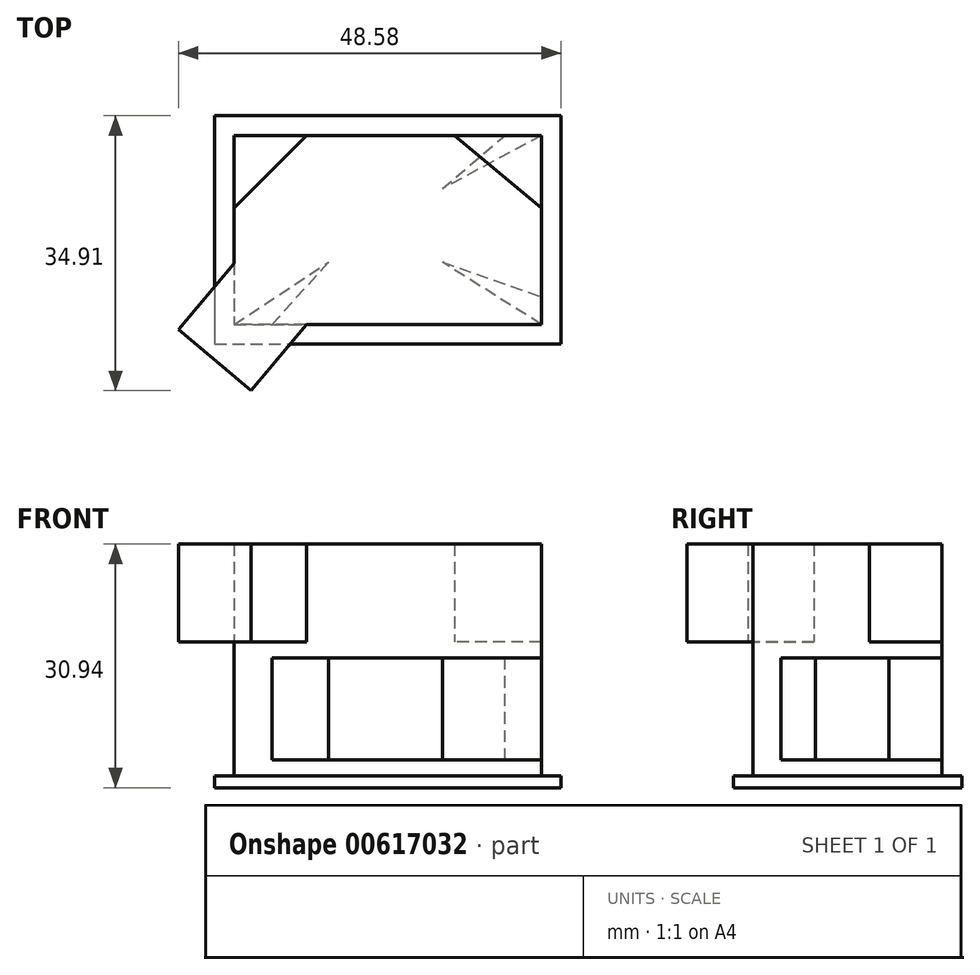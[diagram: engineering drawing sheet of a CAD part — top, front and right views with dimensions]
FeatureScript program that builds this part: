
annotation { "Feature Type Name" : "Feature", "Feature Type Description" : "" }
export const myFeature = defineFeature(function(context is Context, id is Id, definition is map)
    precondition{}
    {
        {
            var Q0;
            Q0=qCreatedBy(makeId("Top.planeOp"),FACE);
            var sketch = newSketch(context, id + "F0", { "sketchPlane" : qUnion([Q0])});
            skLineSegment(sketch, "E0.bottom", {"start": v(-14.47, 23) * mm, "end": v(29.53, 23) * mm});
            skLineSegment(sketch, "E0.top", {"start": v(-14.47, -6) * mm, "end": v(29.53, -6) * mm});
            skLineSegment(sketch, "E0.left", {"start": v(-14.47, 23) * mm, "end": v(-14.47, -6) * mm});
            skLineSegment(sketch, "E0.right", {"start": v(29.53, 23) * mm, "end": v(29.53, -6) * mm});
            skSolve(sketch);
        }
        {
            var Q0;
            Q0 = qSketchRegion(id + "F0", true);
            extrude(context, id + "F1", {"entities" : qUnion([Q0]), "depth" : 1.5 * mm, "offsetDistance" : 25 * mm});
        }
        {
            var Q0;
            Q0=makeQuery(id+"F1.opExtrude","CAP_FACE",FACE,{"disambiguationData":[OSD([sQuery(id+"F0.wireOp",EDGE,"E0.bottom"),sQuery(id+"F0.wireOp",EDGE,"E0.top"),sQuery(id+"F0.wireOp",EDGE,"E0.left"),sQuery(id+"F0.wireOp",EDGE,"E0.right")])],"isStart":false});
            var sketch = newSketch(context, id + "F2", { "sketchPlane" : qUnion([Q0])});
            skLineSegment(sketch, "E1.bottom", {"start": v(-11.97, 20.5) * mm, "end": v(27.03, 20.5) * mm});
            skLineSegment(sketch, "E1.top", {"start": v(-11.97, -3.5) * mm, "end": v(27.03, -3.5) * mm});
            skLineSegment(sketch, "E1.left", {"start": v(-11.97, 20.5) * mm, "end": v(-11.97, -3.5) * mm});
            skLineSegment(sketch, "E1.right", {"start": v(27.03, 20.5) * mm, "end": v(27.03, -3.5) * mm});
            skSolve(sketch);
        }
        {
            var Q0;
            Q0 = qSketchRegion(id + "FiXXtivG3tjkedR_1", true);
            var Q1;
            Q1 = qSketchRegion(id + "F2", true);
            extrude(context, id + "F3", {"entities" : qUnion([Q0, Q1]), "operationType" : NewBodyOperationType.ADD, "depth" : 15 * mm, "offsetDistance" : 25 * mm});
        }
        {
            var Q0;
            Q0=makeQuery(id+"F3.opExtrude","CAP_FACE",FACE,{"disambiguationData":[OSD([sQuery(id+"F2.wireOp",EDGE,"E1.bottom"),sQuery(id+"F2.wireOp",EDGE,"E1.top"),sQuery(id+"F2.wireOp",EDGE,"E1.left"),sQuery(id+"F2.wireOp",EDGE,"E1.right")])],"isStart":false});
            var sketch = newSketch(context, id + "F4", { "sketchPlane" : qUnion([Q0])});
            skLineSegment(sketch, "E2", {"start": v(-11.97, 20.5) * mm, "end": v(-11.97, -3.5) * mm});
            skLineSegment(sketch, "E3", {"start": v(-11.97, -3.5) * mm, "end": v(0, 4.4) * mm});
            skLineSegment(sketch, "E4", {"start": v(0, 4.4) * mm, "end": v(-7.17, -3.5) * mm});
            skLineSegment(sketch, "E5", {"start": v(-7.17, -3.5) * mm, "end": v(27.03, -3.5) * mm});
            skLineSegment(sketch, "E6", {"start": v(27.03, -3.5) * mm, "end": v(14.47, 4.4) * mm});
            skLineSegment(sketch, "E7", {"start": v(14.47, 4.4) * mm, "end": v(27.03, 0) * mm});
            skLineSegment(sketch, "E8", {"start": v(27.03, 0) * mm, "end": v(27.03, 20.5) * mm});
            skLineSegment(sketch, "E9", {"start": v(27.03, 20.5) * mm, "end": v(14.47, 13.73) * mm});
            skLineSegment(sketch, "E10", {"start": v(14.47, 13.73) * mm, "end": v(22.43, 20.5) * mm});
            skLineSegment(sketch, "E11", {"start": v(22.43, 20.5) * mm, "end": v(-11.97, 20.5) * mm});
            skSolve(sketch);
        }
        {
            var Q0;
            Q0 = qSketchRegion(id + "F4", true);
            extrude(context, id + "F5", {"entities" : qUnion([Q0]), "operationType" : NewBodyOperationType.REMOVE, "oppositeDirection" : true, "depth" : 13 * mm, "offsetDistance" : 25 * mm});
        }
        {
            var Q0;
            Q0=makeQuery(id+"F5.boolean.opBoolean","COPY",FACE,{"derivedFrom":makeQuery(id+"F5.opExtrude","CAP_FACE",FACE,{"disambiguationData":[OSD([sQuery(id+"F4.wireOp",EDGE,"E2"),sQuery(id+"F4.wireOp",EDGE,"E3"),sQuery(id+"F4.wireOp",EDGE,"E4"),sQuery(id+"F4.wireOp",EDGE,"E5"),sQuery(id+"F4.wireOp",EDGE,"E6"),sQuery(id+"F4.wireOp",EDGE,"E7"),sQuery(id+"F4.wireOp",EDGE,"E8"),sQuery(id+"F4.wireOp",EDGE,"E9"),sQuery(id+"F4.wireOp",EDGE,"E10"),sQuery(id+"F4.wireOp",EDGE,"E11")])],"isStart":false})});
            var sketch = newSketch(context, id + "F6", { "sketchPlane" : qUnion([Q0])});
            skLineSegment(sketch, "E12", {"start": v(22.43, 20.5) * mm, "end": v(-11.97, 20.5) * mm});
            skLineSegment(sketch, "E13", {"start": v(-11.97, 20.5) * mm, "end": v(-11.97, -3.5) * mm});
            skSolve(sketch);
        }
        {
            var Q0;
            Q0=sQuery(id+"F6.wireOp",EDGE,"E12");
            var Q1;
            Q1=sQuery(id+"F6.wireOp",EDGE,"E13");
            extrude(context, id + "F7", {"bodyType" : ToolBodyType.SURFACE, "surfaceEntities" : qUnion([Q0, Q1]), "depth" : 13 * mm, "offsetDistance" : 25 * mm});
        }
        {
            var Q0;
            Q0=makeQuery(id+"F7.opExtrude","SWEPT_FACE",FACE,{"disambiguationData":[OSD([sQuery(id+"F6.wireOp",EDGE,"E13")])]});
            var sketch = newSketch(context, id + "F8", { "sketchPlane" : qUnion([Q0])});
            skLineSegment(sketch, "E14", {"start": v(-20.5, 16.5) * mm, "end": v(-20.5, 18.54) * mm});
            skLineSegment(sketch, "E15", {"start": v(-20.5, 18.54) * mm, "end": v(3.5, 18.54) * mm});
            skLineSegment(sketch, "E16", {"start": v(3.5, 18.54) * mm, "end": v(3.5, 16.5) * mm});
            skLineSegment(sketch, "E17", {"start": v(3.5, 16.5) * mm, "end": v(-20.5, 16.5) * mm});
            skSolve(sketch);
        }
        {
            var Q0;
            Q0 = qSketchRegion(id + "F8", true);
            extrude(context, id + "F9", {"entities" : qUnion([Q0]), "operationType" : NewBodyOperationType.ADD, "oppositeDirection" : true, "depth" : 39 * mm, "offsetDistance" : 25 * mm});
        }
        {
            var Q0;
            Q0=makeQuery(id+"F9.opExtrude","SWEPT_FACE",FACE,{"disambiguationData":[OSD([sQuery(id+"F8.wireOp",EDGE,"E15")])]});
            var sketch = newSketch(context, id + "F10", { "sketchPlane" : qUnion([Q0])});
            skLineSegment(sketch, "E18", {"start": v(-2.77, 20.5) * mm, "end": v(-11.97, 11.25) * mm});
            skLineSegment(sketch, "E19", {"start": v(-11.97, 11.25) * mm, "end": v(-11.97, 4.24) * mm});
            skLineSegment(sketch, "E20", {"start": v(-11.97, 4.24) * mm, "end": v(-2.77, -3.5) * mm});
            skLineSegment(sketch, "E21", {"start": v(-2.77, -3.5) * mm, "end": v(27.03, -3.5) * mm});
            skLineSegment(sketch, "E22", {"start": v(27.03, -3.5) * mm, "end": v(27.03, 11.25) * mm});
            skLineSegment(sketch, "E23", {"start": v(27.03, 11.25) * mm, "end": v(16.03, 20.5) * mm});
            skLineSegment(sketch, "E24", {"start": v(16.03, 20.5) * mm, "end": v(-2.77, 20.5) * mm});
            skSolve(sketch);
        }
        {
            var Q0;
            Q0 = qSketchRegion(id + "F10", true);
            extrude(context, id + "F11", {"entities" : qUnion([Q0]), "operationType" : NewBodyOperationType.ADD, "depth" : 12.4 * mm, "offsetDistance" : 25 * mm});
        }
        {
            var Q0;
            Q0=makeQuery(id+"F11.opExtrude","SWEPT_FACE",FACE,{"disambiguationData":[OSD([sQuery(id+"F10.wireOp",EDGE,"E20")])]});
            var sketch = newSketch(context, id + "F12", { "sketchPlane" : qUnion([Q0])});
            skLineSegment(sketch, "E25.bottom", {"start": v(-11.89, 30.94) * mm, "end": v(0.14, 30.94) * mm});
            skLineSegment(sketch, "E25.top", {"start": v(-11.89, 18.54) * mm, "end": v(0.14, 18.54) * mm});
            skLineSegment(sketch, "E25.left", {"start": v(-11.89, 30.94) * mm, "end": v(-11.89, 18.54) * mm});
            skLineSegment(sketch, "E25.right", {"start": v(0.14, 30.94) * mm, "end": v(0.14, 18.54) * mm});
            skSolve(sketch);
        }
        {
            var Q0;
            Q0 = qSketchRegion(id + "F12", true);
            extrude(context, id + "F13", {"entities" : qUnion([Q0]), "operationType" : NewBodyOperationType.ADD, "depth" : 11 * mm, "offsetDistance" : 25 * mm});
        }
    });
